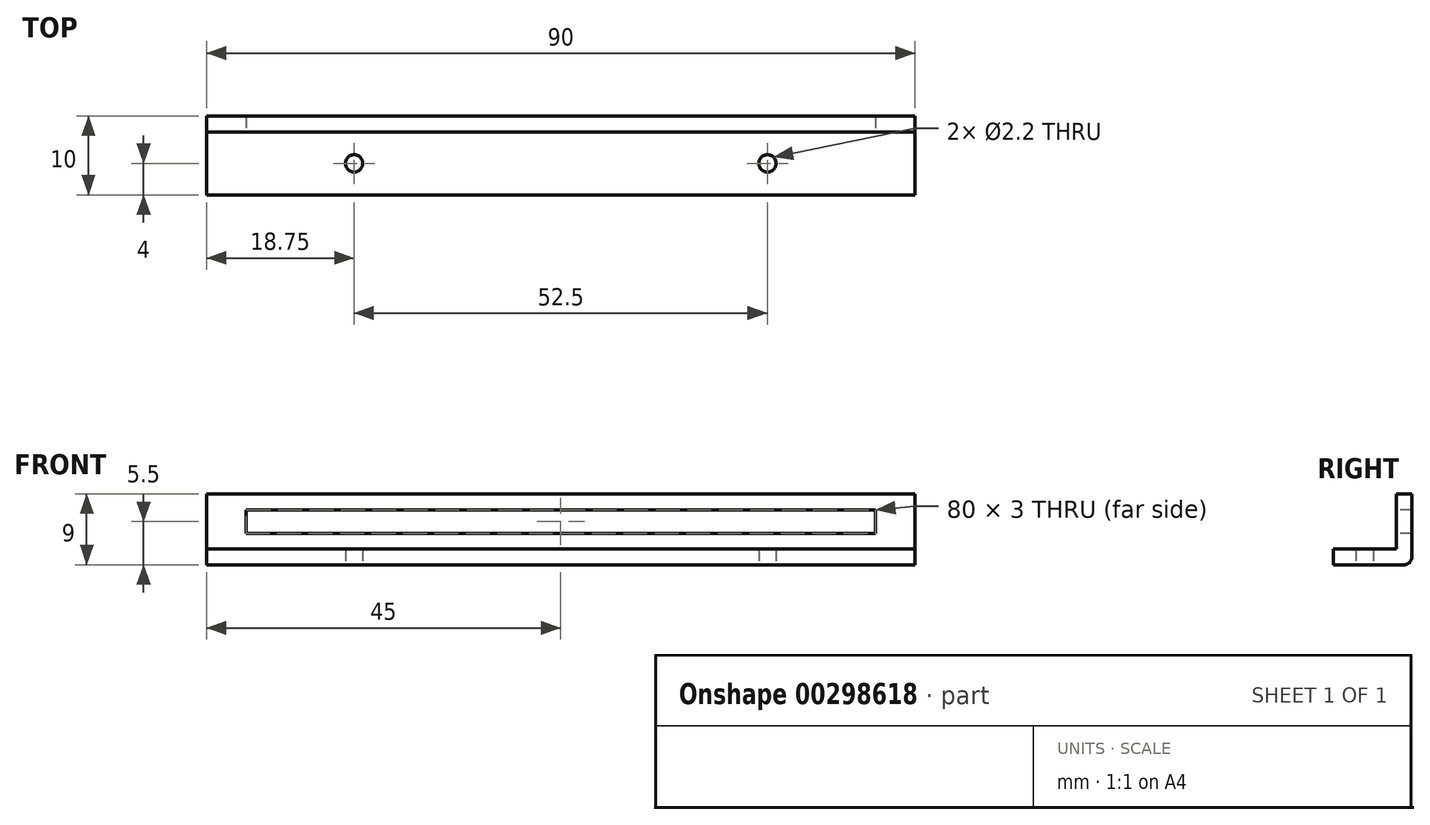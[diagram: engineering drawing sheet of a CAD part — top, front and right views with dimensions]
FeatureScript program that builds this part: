
annotation { "Feature Type Name" : "Feature", "Feature Type Description" : "" }
export const myFeature = defineFeature(function(context is Context, id is Id, definition is map)
    precondition{}
    {
        {
            var Q0;
            Q0=qCreatedBy(makeId("Top.planeOp"),FACE);
            var sketch = newSketch(context, id + "F0", { "sketchPlane" : qUnion([Q0])});
            skLineSegment(sketch, "E0.bottom", {"start": v(45, -5) * mm, "end": v(-45, -5) * mm});
            skLineSegment(sketch, "E0.top", {"start": v(45, 5) * mm, "end": v(-45, 5) * mm});
            skLineSegment(sketch, "E0.left", {"start": v(45, -5) * mm, "end": v(45, 5) * mm});
            skLineSegment(sketch, "E0.right", {"start": v(-45, -5) * mm, "end": v(-45, 5) * mm});
            skPoint(sketch, "E0.middle", {"position": v(0, 0) * mm});
            skCircle(sketch, "E1", {"center": v(-26.25, -1) * mm, "radius": 1.1 * mm});
            skCircle(sketch, "E2", {"center": v(26.25, -1) * mm, "radius": 1.1 * mm});
            skSolve(sketch);
        }
        {
            var Q0;
            Q0 = qSketchRegion(id + "F0", true);
            extrude(context, id + "F1", {"entities" : qUnion([Q0]), "depth" : 2 * mm});
        }
        {
            var Q0;
            Q0=makeQuery(id+"F1.opExtrude","CAP_FACE",FACE,{"disambiguationData":[OSD([sQuery(id+"F0.wireOp",EDGE,"E0.bottom"),sQuery(id+"F0.wireOp",EDGE,"E0.top"),sQuery(id+"F0.wireOp",EDGE,"E0.left"),sQuery(id+"F0.wireOp",EDGE,"E0.right"),sQuery(id+"F0.wireOp",EDGE,"E1"),sQuery(id+"F0.wireOp",EDGE,"E2")])],"isStart":false});
            var sketch = newSketch(context, id + "F2", { "sketchPlane" : qUnion([Q0])});
            skLineSegment(sketch, "E3.bottom", {"start": v(-45, 5) * mm, "end": v(45, 5) * mm});
            skLineSegment(sketch, "E3.top", {"start": v(-45, 3) * mm, "end": v(45, 3) * mm});
            skLineSegment(sketch, "E3.left", {"start": v(-45, 3) * mm, "end": v(-45, 5) * mm});
            skLineSegment(sketch, "E3.right", {"start": v(45, 3) * mm, "end": v(45, 5) * mm});
            skSolve(sketch);
        }
        {
            var Q0;
            Q0 = qSketchRegion(id + "F2", true);
            extrude(context, id + "F3", {"entities" : qUnion([Q0]), "operationType" : NewBodyOperationType.ADD, "depth" : 7 * mm});
        }
        {
            var Q0;
            Q0=makeQuery(id+"F1.opExtrude","CAP_EDGE",EDGE,{"disambiguationData":[OSD([sQuery(id+"F0.wireOp",EDGE,"E0.top")])],"isStart":true});
            var Q1;
            Q1=makeQuery(id+"F3.opExtrude","CAP_EDGE",EDGE,{"disambiguationData":[OSD([sQuery(id+"F2.wireOp",EDGE,"E3.top")])],"isStart":true});
            fillet(context, id + "F4", {"entities" : qUnion([Q0, Q1]), "radius" : 1 * mm, "tangentPropagation" : true, "allowEdgeOverflow" : false});
        }
        {
            var Q0;
            Q0=makeQuery(id+"F3.opExtrude","SWEPT_FACE",FACE,{"disambiguationData":[OSD([sQuery(id+"F2.wireOp",EDGE,"E3.top")])]});
            var sketch = newSketch(context, id + "F5", { "sketchPlane" : qUnion([Q0])});
            skLineSegment(sketch, "E4.bottom", {"start": v(40, 4) * mm, "end": v(-40, 4) * mm});
            skLineSegment(sketch, "E4.top", {"start": v(40, 7) * mm, "end": v(-40, 7) * mm});
            skLineSegment(sketch, "E4.left", {"start": v(40, 4) * mm, "end": v(40, 7) * mm});
            skLineSegment(sketch, "E4.right", {"start": v(-40, 4) * mm, "end": v(-40, 7) * mm});
            skPoint(sketch, "E4.middle", {"position": v(0, 5.5) * mm});
            skSolve(sketch);
        }
        {
            var Q0;
            Q0 = qSketchRegion(id + "F5", true);
            extrude(context, id + "F6", {"entities" : qUnion([Q0]), "operationType" : NewBodyOperationType.REMOVE, "oppositeDirection" : true, "depth" : 2 * mm});
        }
    });
